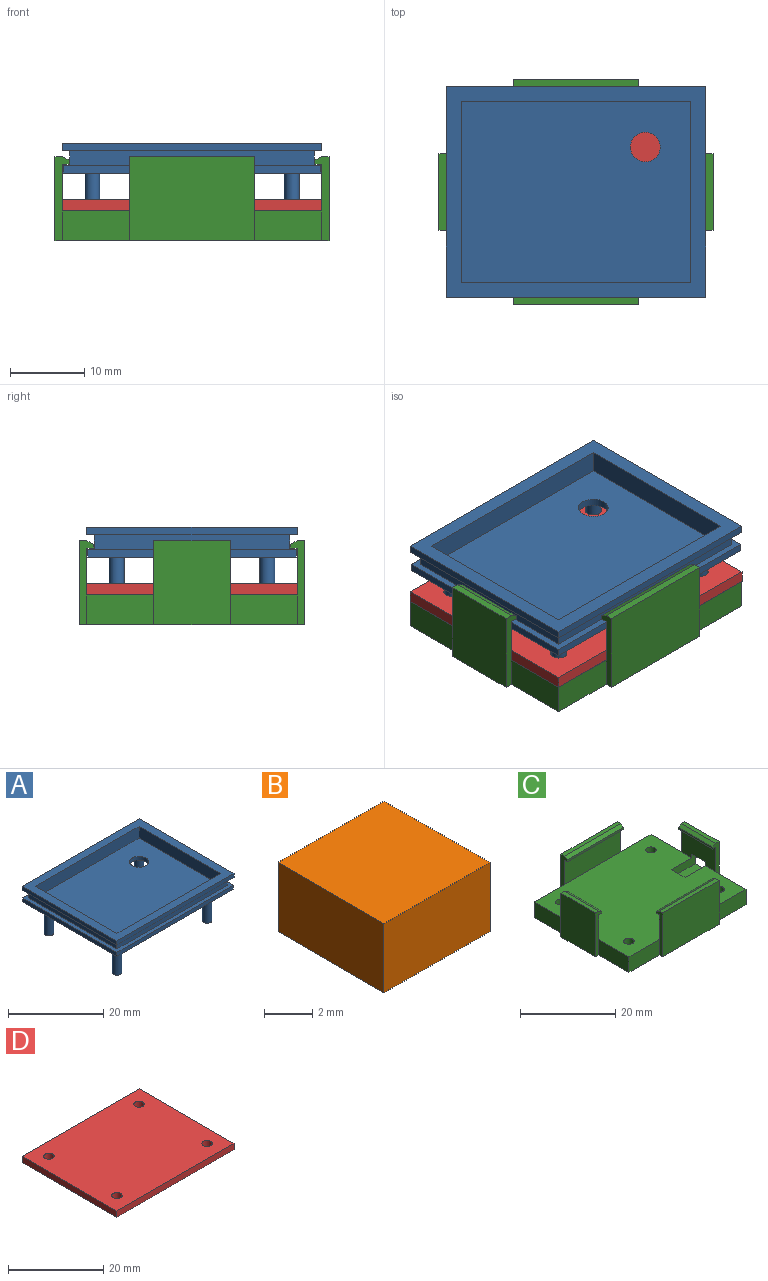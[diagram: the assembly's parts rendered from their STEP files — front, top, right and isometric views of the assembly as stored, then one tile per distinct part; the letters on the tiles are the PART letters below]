
ASSEMBLY  parts=4 mates=7
PART A: 30 faces, bbox 34.8x28.3x12.1 mm
  f0: plane 34.6x28.05mm, normal (0,0,1), area 109.5mm2, adj f1,f12,f14,f15,f16,f17,f18,f19
  f1: plane 26.25x2mm, normal (1,0,0), area 52.5mm2, adj f0,f13,f14,f15
  f2: plane 34.8x1mm, normal (0,-1,0), area 34.8mm2, adj f3,f5,f6,f13
  f3: plane 28.25x1mm, normal (1,0,0), area 28.2mm2, adj f2,f4,f6,f13
  f4: plane 34.8x1mm, normal (0,1,0), area 34.8mm2, adj f3,f5,f6,f13
  f5: plane 28.25x1mm, normal (-1,0,0), area 28.2mm2, adj f2,f4,f6,f13
  f6: plane 34.8x28.25mm, normal (0,0,1), area 236.2mm2, adj f2,f3,f4,f5,f8,f9,f10,f11
  f7: plane 30.8x24.25mm, normal (0,0,1), area 734.3mm2, adj f8,f9,f10,f11,f29
  f8: plane 30.8x3mm, normal (0,1,0), area 92.4mm2, adj f6,f7,f9,f11
  f9: plane 24.25x3mm, normal (-1,0,0), area 72.8mm2, adj f6,f7,f8,f10
  f10: plane 30.8x3mm, normal (0,-1,0), area 92.4mm2, adj f6,f7,f9,f11
  f11: plane 24.25x3mm, normal (1,0,0), area 72.8mm2, adj f6,f7,f8,f10
  f12: plane 26.25x2mm, normal (-1,0,0), area 52.5mm2, adj f0,f13,f14,f15
  f13: plane 34.8x28.25mm, normal (0,0,-1), area 122.1mm2, adj f1,f2,f3,f4,f5,f12,f14,f15
  f14: plane 32.8x2mm, normal (0,-1,0), area 65.6mm2, adj f0,f1,f12,f13
  f15: plane 32.8x2mm, normal (0,1,0), area 65.6mm2, adj f0,f1,f12,f13
  f16: plane 28.05x1mm, normal (1,0,0), area 28.1mm2, adj f0,f17,f18,f28
  f17: plane 34.6x1mm, normal (0,1,0), area 34.6mm2, adj f0,f16,f19,f28
  f18: plane 34.6x1mm, normal (0,-1,0), area 34.6mm2, adj f0,f16,f19,f28
  f19: plane 28.05x1mm, normal (-1,0,0), area 28.1mm2, adj f0,f17,f18,f28
  f20: plane 2x2mm, normal (0,0,-1), area 3.1mm2, adj f24
  f21: plane 2x2mm, normal (0,0,-1), area 3.1mm2, adj f25
  f22: plane 2x2mm, normal (0,0,-1), area 3.1mm2, adj f26
  f23: plane 2x2mm, normal (0,0,-1), area 3.1mm2, adj f27
  f24: cylinder r=1mm len=8.1mm, axis (0,0,1), area 50.9mm2, adj f20,f28
  f25: cylinder r=1mm len=8.1mm, axis (0,0,1), area 50.9mm2, adj f21,f28
  f26: cylinder r=1mm len=8.1mm, axis (0,0,1), area 50.9mm2, adj f22,f28
  f27: cylinder r=1mm len=8.1mm, axis (0,0,1), area 50.9mm2, adj f23,f28
  f28: plane 34.6x28.05mm, normal (0,0,-1), area 945.4mm2, adj f16,f17,f18,f19,f24,f25,f26,f27
  f29: cylinder r=2mm len=4mm, axis (0,0,-1), area 12.6mm2, adj f7,f28
PART B: 6 faces, bbox 6.2x6.2x3.5 mm
  f0: plane 6.2x3.5mm, normal (0,1,0), area 21.7mm2, adj f1,f3,f4,f5
  f1: plane 6.2x3.5mm, normal (-1,0,0), area 21.7mm2, adj f0,f2,f4,f5
  f2: plane 6.2x3.5mm, normal (0,-1,0), area 21.7mm2, adj f1,f3,f4,f5
  f3: plane 6.2x3.5mm, normal (1,0,0), area 21.7mm2, adj f0,f2,f4,f5
  f4: plane 6.2x6.2mm, normal (0,0,1), area 38.4mm2, adj f0,f1,f2,f3
  f5: plane 6.2x6.2mm, normal (0,0,-1), area 38.4mm2, adj f0,f1,f2,f3
PART C: 59 faces, bbox 36.8x30.3x11.3 mm
  f0: plane 16.8x6.3mm, normal (0,-1,0), area 105.8mm2, adj f9,f20,f26,f36
  f1: plane 10.25x6.3mm, normal (1,0,0), area 64.6mm2, adj f9,f21,f25,f32
  f2: plane 16.8x6.3mm, normal (0,1,0), area 105.8mm2, adj f9,f16,f22,f38
  f3: plane 10.25x6.3mm, normal (-1,0,0), area 60.6mm2, adj f9,f17,f29,f42,f54,f56,f57
  f4: plane 11.3x10.25mm, normal (1,0,0), area 103.8mm2, adj f8,f17,f29,f45,f54,f55,f56,f57
  f5: plane 16.8x11.3mm, normal (0,-1,0), area 189.8mm2, adj f8,f16,f22,f41
  f6: plane 11.3x10.25mm, normal (-1,0,0), area 115.8mm2, adj f8,f21,f25,f33
  f7: plane 16.8x11.3mm, normal (0,1,0), area 189.8mm2, adj f8,f20,f26,f37
  f8: plane 36.8x30.25mm, normal (0,0,-1), area 989.8mm2, adj f4,f5,f6,f7,f10,f11,f12,f13
  f9: plane 34.8x28.25mm, normal (0,0,1), area 943.9mm2, adj f0,f1,f2,f3,f10,f11,f12,f13
  f10: cylinder r=1.1mm len=4mm, axis (0,0,1), area 27.6mm2, adj f8,f9
  f11: cylinder r=1.1mm len=4mm, axis (0,0,1), area 27.6mm2, adj f8,f9
  f12: cylinder r=1.1mm len=4mm, axis (0,0,1), area 27.6mm2, adj f8,f9
  f13: cylinder r=1.1mm len=4mm, axis (0,0,1), area 27.6mm2, adj f8,f9
  f14: plane 9x4mm, normal (1,0,0), area 36mm2, adj f8,f9,f15,f17
  f15: plane 9x4mm, normal (0,-1,0), area 36mm2, adj f8,f9,f14,f16
  f16: plane 11.3x1.9mm, normal (1,0,0), area 12mm2, adj f2,f5,f8,f15,f38,f39,f40,f41
  f17: plane 11.3x1.9mm, normal (0,-1,0), area 12mm2, adj f3,f4,f8,f14,f42,f43,f44,f45
  f18: plane 9x4mm, normal (-1,0,0), area 36mm2, adj f8,f9,f19,f21
  f19: plane 9x4mm, normal (0,1,0), area 36mm2, adj f8,f9,f18,f20
  f20: plane 11.3x1.9mm, normal (-1,0,0), area 12mm2, adj f0,f7,f8,f19,f34,f35,f36,f37
  f21: plane 11.3x1.9mm, normal (0,1,0), area 12mm2, adj f1,f6,f8,f18,f30,f31,f32,f33
  f22: plane 11.3x1.9mm, normal (-1,0,0), area 12mm2, adj f2,f5,f8,f23,f38,f39,f40,f41
  f23: plane 9x4mm, normal (0,-1,0), area 36mm2, adj f8,f9,f22,f24
  f24: plane 9x4mm, normal (-1,0,0), area 36mm2, adj f8,f9,f23,f25
  f25: plane 11.3x1.9mm, normal (0,-1,0), area 12mm2, adj f1,f6,f8,f24,f30,f31,f32,f33
  f26: plane 11.3x1.9mm, normal (1,0,0), area 12mm2, adj f0,f7,f8,f27,f34,f35,f36,f37
  f27: plane 9x4mm, normal (0,1,0), area 36mm2, adj f8,f9,f26,f28
  f28: plane 9x4mm, normal (1,0,0), area 36mm2, adj f8,f9,f27,f29
  f29: plane 11.3x1.9mm, normal (0,1,0), area 12mm2, adj f3,f4,f8,f28,f42,f43,f44,f45
  f30: plane 10.25x0.5mm, normal (1,0,0), area 5.1mm2, adj f21,f25,f31,f32
  f31: plane 10.25x0.9mm, normal (0.49,0,0.87), area 10.6mm2, adj f21,f25,f30,f33
  f32: plane 10.25x0.9mm, normal (0,0,-1), area 9.2mm2, adj f1,f21,f25,f30
  f33: plane 10.25x1mm, normal (0,0,1), area 10.3mm2, adj f6,f21,f25,f31
  f34: plane 16.8x0.5mm, normal (0,-1,0), area 8.4mm2, adj f20,f26,f35,f36
  f35: plane 16.8x0.9mm, normal (0,-0.49,0.87), area 17.3mm2, adj f20,f26,f34,f37
  f36: plane 16.8x0.9mm, normal (0,0,-1), area 15.1mm2, adj f0,f20,f26,f34
  f37: plane 16.8x1mm, normal (0,0,1), area 16.8mm2, adj f7,f20,f26,f35
  f38: plane 16.8x0.9mm, normal (0,0,-1), area 15.1mm2, adj f2,f16,f22,f39
  f39: plane 16.8x0.5mm, normal (0,1,0), area 8.4mm2, adj f16,f22,f38,f40
  f40: plane 16.8x0.9mm, normal (0,0.49,0.87), area 17.3mm2, adj f16,f22,f39,f41
  f41: plane 16.8x1mm, normal (0,0,1), area 16.8mm2, adj f5,f16,f22,f40
  f42: plane 10.25x0.9mm, normal (0,0,-1), area 9.2mm2, adj f3,f17,f29,f43
  f43: plane 10.25x0.5mm, normal (-1,0,0), area 5.1mm2, adj f17,f29,f42,f44
  f44: plane 10.25x0.9mm, normal (-0.49,0,0.87), area 10.6mm2, adj f17,f29,f43,f45
  f45: plane 10.25x1mm, normal (0,0,1), area 10.3mm2, adj f4,f17,f29,f44
  f46: cylinder r=1.6mm len=3.2mm, axis (0,0,-1), area 32.2mm2, adj f8,f47
  f47: plane 3.2x3.2mm, normal (0,0,-1), area 8mm2, adj f46
  f48: cylinder r=1.6mm len=3.2mm, axis (0,0,-1), area 32.2mm2, adj f8,f49
  f49: plane 3.2x3.2mm, normal (0,0,-1), area 8mm2, adj f48
  f50: cylinder r=1.6mm len=3.2mm, axis (0,0,-1), area 32.2mm2, adj f8,f51
  f51: plane 3.2x3.2mm, normal (0,0,-1), area 8mm2, adj f50
  f52: cylinder r=1.6mm len=3.2mm, axis (0,0,-1), area 32.2mm2, adj f8,f53
  f53: plane 3.2x3.2mm, normal (0,0,-1), area 8mm2, adj f52
  f54: plane 7x3mm, normal (0,1,0), area 15mm2, adj f3,f4,f9,f55,f57,f58
  f55: plane 7x4mm, normal (0,0,1), area 28mm2, adj f4,f54,f56,f58
  f56: plane 7x3mm, normal (0,-1,0), area 15mm2, adj f3,f4,f9,f55,f57,f58
  f57: plane 4x1mm, normal (0,0,-1), area 4mm2, adj f3,f4,f54,f56
  f58: plane 4x2mm, normal (1,0,0), area 8mm2, adj f9,f54,f55,f56
PART D: 10 faces, bbox 34.8x28.3x1.6 mm
  f0: plane 28.25x1.6mm, normal (-1,0,0), area 45.2mm2, adj f1,f3,f4,f5
  f1: plane 34.8x1.6mm, normal (0,-1,0), area 55.7mm2, adj f0,f2,f4,f5
  f2: plane 28.25x1.6mm, normal (1,0,0), area 45.2mm2, adj f1,f3,f4,f5
  f3: plane 34.8x1.6mm, normal (0,1,0), area 55.7mm2, adj f0,f2,f4,f5
  f4: plane 34.8x28.25mm, normal (0,0,1), area 967.9mm2, adj f0,f1,f2,f3,f6,f7,f8,f9
  f5: plane 34.8x28.25mm, normal (0,0,-1), area 967.9mm2, adj f0,f1,f2,f3,f6,f7,f8,f9
  f6: cylinder r=1.1mm len=2.2mm, axis (0,0,1), area 11.1mm2, adj f4,f5
  f7: cylinder r=1.1mm len=2.2mm, axis (0,0,1), area 11.1mm2, adj f4,f5
  f8: cylinder r=1.1mm len=2.2mm, axis (0,0,1), area 11.1mm2, adj f4,f5
  f9: cylinder r=1.1mm len=2.2mm, axis (0,0,1), area 11.1mm2, adj f4,f5
PLACE A t=(-7.24,21.71,51.36)mm
PLACE B t=(-6.67,21.75,47.86)mm
PLACE C t=(-7.24,21.71,42.26)mm
PLACE D t=(-7.24,21.71,46.26)mm
MATE planar B.f5 <-> D.f4  axis (0,0,-1) through (-6.67,21.75,47.86)mm
MATE planar C.f23 <-> A.f2  axis (0,-1,0) through (-20.14,7.58,44.26)mm
MATE planar D.f0 <-> C.f24  axis (-1,0,0) through (-24.64,21.71,47.06)mm
MATE planar C.f9 <-> D.f5  axis (0,0,1) through (-7.61,21.71,46.26)mm
MATE planar D.f1 <-> C.f23  axis (0,-1,0) through (-7.24,7.58,47.06)mm
MATE planar B.f4 <-> A.f28  axis (0,0,1) through (-6.67,21.75,51.36)mm
MATE planar C.f24 <-> A.f5  axis (-1,0,0) through (-24.64,12.08,44.26)mm
